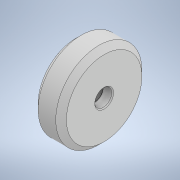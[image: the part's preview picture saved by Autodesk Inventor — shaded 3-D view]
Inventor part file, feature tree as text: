
AUTODESK INVENTOR PART (.ipt)
format: ipt  version: 2022 (Build 260153000, 153)  size: 153,088 bytes
history: native  units: mm
features: sketch x4, revolve x2, hole x2, other x1
ambient origin geometry x8: Origin, YZ Plane, XZ Plane, XY Plane, X Axis, Y Axis, Z Axis, Center Point
bodies: Body1 (feature_tree)
feature tree (9):
  other  "Твердое тело1"
  revolve  "Вращение1"
  hole  "Отверстие1"  [1 undecoded]
  revolve  "Вращение2"
  hole  "Отверстие2"  [1 undecoded]
  sketch  "Эскиз1"
  sketch  "Эскиз2"
  sketch  "Эскиз3"
  sketch  "Эскиз4"
note: 2 required parameter values undecoded (feature->parameter linkage not recoverable at this tier; creation-order binding heuristic only, values carry confidence <= 0.55)
